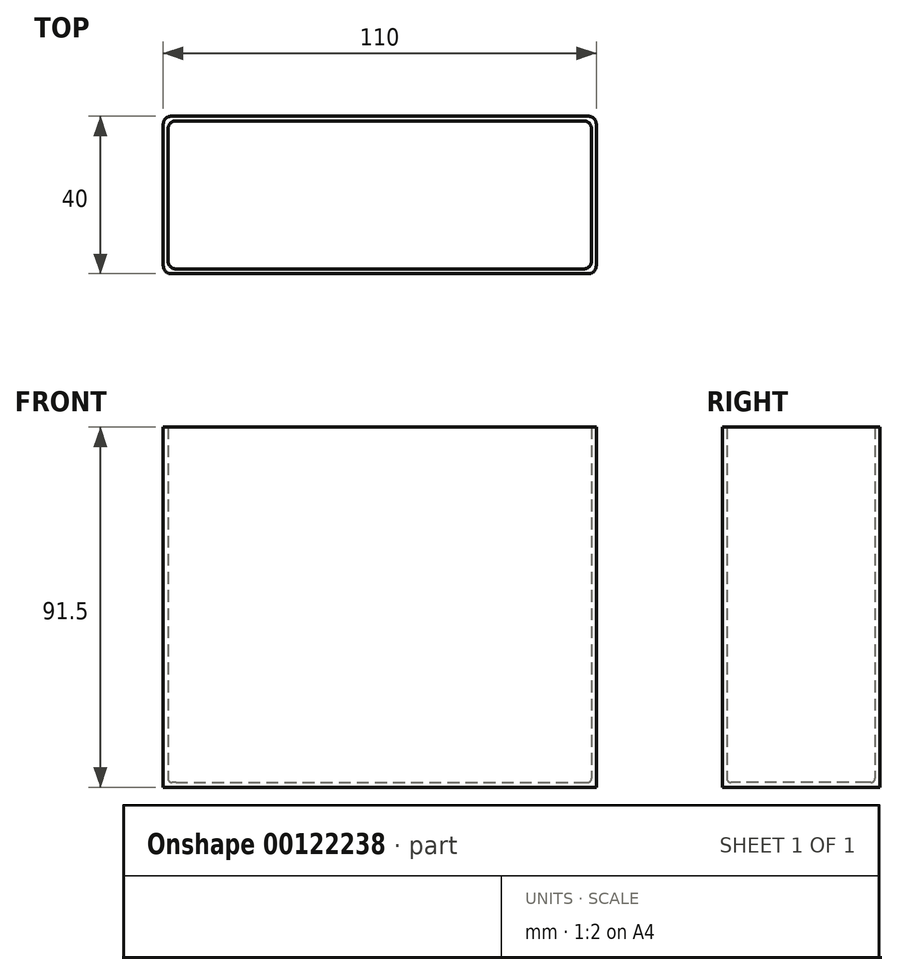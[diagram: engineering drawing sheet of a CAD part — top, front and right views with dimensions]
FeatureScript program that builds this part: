
annotation { "Feature Type Name" : "Feature", "Feature Type Description" : "" }
export const myFeature = defineFeature(function(context is Context, id is Id, definition is map)
    precondition{}
    {
        {
            var Q0;
            Q0=qCreatedBy(makeId("Top.planeOp"),FACE);
            var sketch = newSketch(context, id + "F0", { "sketchPlane" : qUnion([Q0])});
            skLineSegment(sketch, "E0.bottom", {"start": v(-73.3, -6.76) * mm, "end": v(36.7, -6.76) * mm});
            skLineSegment(sketch, "E0.top", {"start": v(-73.3, -46.76) * mm, "end": v(36.7, -46.76) * mm});
            skLineSegment(sketch, "E0.left", {"start": v(-73.3, -6.76) * mm, "end": v(-73.3, -46.76) * mm});
            skLineSegment(sketch, "E0.right", {"start": v(36.7, -6.76) * mm, "end": v(36.7, -46.76) * mm});
            skLineSegment(sketch, "E1.bottom", {"start": v(-72.1, -7.96) * mm, "end": v(35.5, -7.96) * mm});
            skLineSegment(sketch, "E1.top", {"start": v(-72.1, -45.56) * mm, "end": v(35.5, -45.56) * mm});
            skLineSegment(sketch, "E1.left", {"start": v(-72.1, -7.96) * mm, "end": v(-72.1, -45.56) * mm});
            skLineSegment(sketch, "E1.right", {"start": v(35.5, -7.96) * mm, "end": v(35.5, -45.56) * mm});
            skPoint(sketch, "E2", {"position": v(35.5, -26.76) * mm});
            skPoint(sketch, "E3", {"position": v(-18.3, -45.56) * mm});
            skSolve(sketch);
        }
        {
            var Q0;
            Q0=makeQuery(id+"F0.imprint","IMPRINT",FACE,{"disambiguationData":[TD([[makeQuery(id+"F0.imprint","IMPRINT",EDGE,{"derivedFrom":sQuery(id+"F0.wireOp",EDGE,"E0.bottom")}),-1.0]])]});
            extrude(context, id + "F1", {"entities" : qUnion([Q0]), "depth" : 91.5 * mm});
        }
        {
            var Q0;
            Q0=makeQuery(id+"F0.imprint","IMPRINT",FACE,{"disambiguationData":[TD([[makeQuery(id+"F0.imprint","IMPRINT",EDGE,{"derivedFrom":sQuery(id+"F0.wireOp",EDGE,"E0.bottom")}),-1.0]])]});
            var Q1;
            Q1=makeQuery(id+"F0.imprint","IMPRINT",FACE,{"disambiguationData":[TD([[makeQuery(id+"F0.imprint","IMPRINT",EDGE,{"derivedFrom":sQuery(id+"F0.wireOp",EDGE,"E1.bottom")}),-1.0]])]});
            extrude(context, id + "F2", {"entities" : qUnion([Q0, Q1]), "operationType" : NewBodyOperationType.ADD, "depth" : 1.2 * mm});
        }
        {
            var Q0;
            Q0=makeQuery(id+"F1.opExtrude","SWEPT_EDGE",EDGE,{"disambiguationData":[OSD([sQuery(id+"F0.wireOp",EDGE,"E0.top"),sQuery(id+"F0.wireOp",EDGE,"E0.left")])]});
            var Q1;
            Q1=makeQuery(id+"F1.opExtrude","SWEPT_EDGE",EDGE,{"disambiguationData":[OSD([sQuery(id+"F0.wireOp",EDGE,"E0.top"),sQuery(id+"F0.wireOp",EDGE,"E0.right")])]});
            var Q2;
            Q2=makeQuery(id+"F1.opExtrude","SWEPT_EDGE",EDGE,{"disambiguationData":[OSD([sQuery(id+"F0.wireOp",EDGE,"E0.bottom"),sQuery(id+"F0.wireOp",EDGE,"E0.right")])]});
            var Q3;
            Q3=makeQuery(id+"F1.opExtrude","SWEPT_EDGE",EDGE,{"disambiguationData":[OSD([sQuery(id+"F0.wireOp",EDGE,"E0.bottom"),sQuery(id+"F0.wireOp",EDGE,"E0.left")])]});
            var Q4;
            Q4=makeQuery(id+"F1.opExtrude","SWEPT_EDGE",EDGE,{"disambiguationData":[OSD([sQuery(id+"F0.wireOp",EDGE,"E1.bottom"),sQuery(id+"F0.wireOp",EDGE,"E1.right")])]});
            var Q5;
            Q5=makeQuery(id+"F1.opExtrude","SWEPT_EDGE",EDGE,{"disambiguationData":[OSD([sQuery(id+"F0.wireOp",EDGE,"E1.bottom"),sQuery(id+"F0.wireOp",EDGE,"E1.left")])]});
            var Q6;
            Q6=makeQuery(id+"F1.opExtrude","SWEPT_EDGE",EDGE,{"disambiguationData":[OSD([sQuery(id+"F0.wireOp",EDGE,"E1.top"),sQuery(id+"F0.wireOp",EDGE,"E1.left")])]});
            var Q7;
            Q7=makeQuery(id+"F1.opExtrude","SWEPT_EDGE",EDGE,{"disambiguationData":[OSD([sQuery(id+"F0.wireOp",EDGE,"E1.top"),sQuery(id+"F0.wireOp",EDGE,"E1.right")])]});
            fillet(context, id + "F3", {"entities" : qUnion([Q0, Q1, Q2, Q3, Q4, Q5, Q6, Q7]), "radius" : 2 * mm, "tangentPropagation" : true, "allowEdgeOverflow" : false});
        }
        {
            var Q0;
            Q0=makeQuery(id+"F2.boolean.opBoolean","INTERSECT",EDGE,{"derivedFrom":[makeQuery(id+"F1.opExtrude","SWEPT_FACE",FACE,{"disambiguationData":[OSD([sQuery(id+"F0.wireOp",EDGE,"E1.left")])]}),makeQuery(id+"F2.opExtrude","CAP_FACE",FACE,{"disambiguationData":[OSD([sQuery(id+"F0.wireOp",EDGE,"E0.bottom"),sQuery(id+"F0.wireOp",EDGE,"E0.top"),sQuery(id+"F0.wireOp",EDGE,"E0.left"),sQuery(id+"F0.wireOp",EDGE,"E0.right")])],"isStart":false})]});
            fillet(context, id + "F4", {"entities" : qUnion([Q0]), "radius" : 1 * mm, "tangentPropagation" : true, "allowEdgeOverflow" : false});
        }
    });
